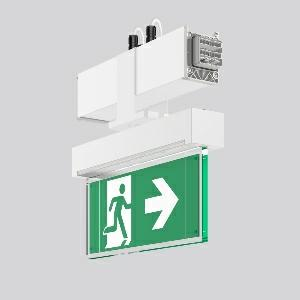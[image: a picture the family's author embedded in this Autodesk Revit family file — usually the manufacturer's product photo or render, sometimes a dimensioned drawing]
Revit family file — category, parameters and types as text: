
# Revit family: linedo_module_rz_9503rz_762_409_023_d036
name_source: partatom
category: Lighting Fixtures
units: mm (PartAtom-declared; Revit-internal decimal feet)

## family parameters
Cut with Voids When Loaded = No
Host = Face
Light Source = No
Part Type = Normal
Room Calculation Point = No
Round Connector Dimension = Use Diameter
Shared = No

## types (1)
- LINEDO Module RZ
    Apparent Load = 0 VA
    Default Elevation = 1800 mm
    Description = LINEDO, white, on/off
Continuous line luminaire, L 336 B 62 H 308, CBS, AC-Control
    Height = 308 mm
    Lamp = 0 x
    Length = 336 mm
    Luminous efficacy = 0 lm/W
    Manufacturer = RZB
    ModVariant = No
    Model = 9503RZ.762.409.023
    Mounting Place = Ceiling
    Mounting Type = Surface mounted
    Number of Poles = 1
    OnlyDefault = Yes
    Power Factor = 1
    Product Name = LINEDO Module RZ
    Product group = Continuous line luminaire system Linedo IP 54
    ProductGroupID = 314
    Protection Class = Protection class I
    Protection Degree = IP 54
    RLX_Detail_Level = 1
    RLX_Emergency_Light_Flux = 0 lm
    RLX_Emergency_Type = 0
    RLX_Emergency_Type_DB = No
    RlxData = <blob elided: 33073 chars, md5=dddc2c35>
    Standby Power = 0 W
    System Light Flux = 0 lm
    System Power = 0 W
    Type Comments = Product without accessories
    Type Image = 9503rz.762.434.023.jpg
    URL = http://relux.com
    VarID = ---
    Voltage = 0 V
    Weight = 0.00 kg
    Width = 62 mm  [stored 0.203412 ft]

note: [stored X ft] marks values corroborated as IEEE doubles in the binary element streams (Revit-internal decimal feet)

## geometry (parser evidence)
native form markers: Blend x4, Sweep x13
no freeform markers — native parametric forms only
